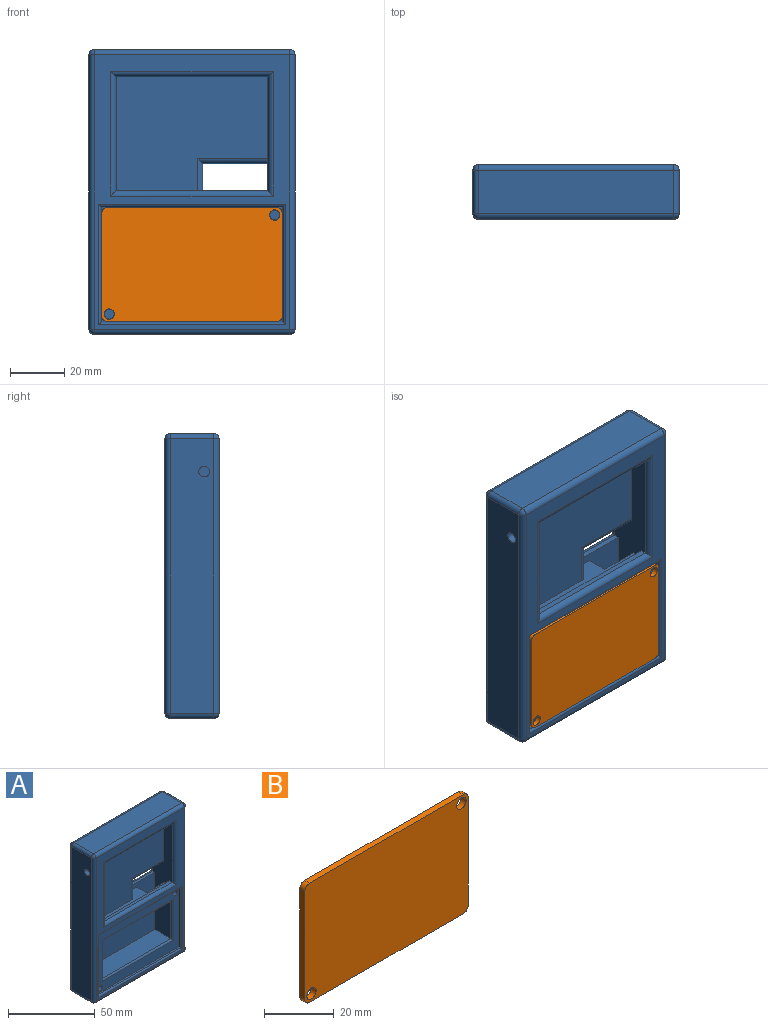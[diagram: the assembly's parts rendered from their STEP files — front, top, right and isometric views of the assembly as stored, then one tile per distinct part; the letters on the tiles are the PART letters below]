
ASSEMBLY  parts=2 mates=1
PART A: 70 faces, bbox 76x20x105 mm
  f0: plane 101x72mm, normal (0,-1,0), area 1441.5mm2, adj f29,f30,f39,f40,f46,f47,f48,f49
  f1: plane 24x2mm, normal (0,0,1), area 48mm2, adj f8,f17,f18,f24
  f2: plane 10.5x8mm, normal (1,0,0), area 84mm2, adj f3,f7,f17,f51
  f3: plane 15x10.5mm, normal (0,1,0), area 157.5mm2, adj f2,f7,f8,f51
  f4: plane 56x45mm, normal (0,-1,0), area 2130mm2, adj f8,f9,f10,f20,f21,f51
  f5: plane 101x72mm, normal (0,1,0), area 6880mm2, adj f22,f23,f24,f25,f32,f33,f41,f42
  f6: plane 27x13mm, normal (1,0,0), area 351mm2, adj f7,f16,f17,f63
  f7: plane 56x13mm, normal (0,0,-1), area 608mm2, adj f2,f3,f6,f8,f17,f62
  f8: plane 82.5x16mm, normal (-1,0,0), area 855.9mm2, adj f1,f3,f4,f7,f10,f14,f16,f17
  f9: plane 45x7mm, normal (1,0,0), area 296.4mm2, adj f4,f10,f14,f47,f50,f51,f52
  f10: plane 56x7mm, normal (0,0,-1), area 392mm2, adj f4,f8,f9,f46
  f11: plane 101x16mm, normal (1,0,0), area 1616mm2, adj f34,f39,f42,f45
  f12: plane 72x16mm, normal (0,0,1), area 1152mm2, adj f31,f40,f41,f45
  f13: plane 101x16mm, normal (-1,0,0), area 1603.4mm2, adj f26,f30,f31,f32,f52
  f14: plane 56x2mm, normal (0,0,1), area 112mm2, adj f8,f9,f49,f50
  f15: plane 72x16mm, normal (0,0,-1), area 1152mm2, adj f26,f29,f33,f34
  f16: plane 56x13mm, normal (0,0,1), area 728mm2, adj f6,f8,f17,f65
  f17: plane 56x40.5mm, normal (0,-1,0), area 1741.5mm2, adj f1,f2,f6,f7,f8,f16,f18,f51
  f18: plane 13x7mm, normal (1,0,0), area 85mm2, adj f1,f17,f19,f21,f22,f51
  f19: plane 24x7mm, normal (0,0,-1), area 168mm2, adj f8,f18,f20,f23
  f20: cylinder r=2mm len=26mm, axis (1,0,0), area 77.7mm2, adj f4,f8,f19,f21
  f21: cylinder r=2mm len=15mm, axis (0,0,1), area 43.1mm2, adj f4,f18,f20,f51
  f22: cylinder r=2mm len=14mm, axis (0,0,-1), area 36mm2, adj f5,f18,f23,f24
  f23: cylinder r=2mm len=28mm, axis (-1,0,0), area 80mm2, adj f5,f19,f22,f25
  f24: cylinder r=2mm len=28mm, axis (-1,0,0), area 80mm2, adj f1,f5,f22,f25
  f25: cylinder r=2mm len=14mm, axis (0,0,-1), area 36mm2, adj f5,f8,f23,f24
  f26: cylinder r=2mm len=16mm, axis (0,-1,0), area 50.3mm2, adj f13,f15,f27,f28
  f27: sphere r=2mm, area 6.3mm2, adj f26,f29,f30
  f28: sphere r=2mm, area 6.3mm2, adj f26,f32,f33
  f29: cylinder r=2mm len=72mm, axis (-1,0,0), area 226.2mm2, adj f0,f15,f27,f35
  f30: cylinder r=2mm len=101mm, axis (0,0,1), area 317.3mm2, adj f0,f13,f27,f36
  f31: cylinder r=2mm len=16mm, axis (0,1,0), area 50.3mm2, adj f12,f13,f36,f37
  f32: cylinder r=2mm len=101mm, axis (0,0,-1), area 317.3mm2, adj f5,f13,f28,f37
  f33: cylinder r=2mm len=72mm, axis (1,0,0), area 226.2mm2, adj f5,f15,f28,f38
  f34: cylinder r=2mm len=16mm, axis (0,1,0), area 50.3mm2, adj f11,f15,f35,f38
  f35: sphere r=2mm, area 6.3mm2, adj f29,f34,f39
  f36: sphere r=2mm, area 6.3mm2, adj f30,f31,f40
  f37: sphere r=2mm, area 6.3mm2, adj f31,f32,f41
  f38: sphere r=2mm, area 6.3mm2, adj f33,f34,f42
  f39: cylinder r=2mm len=101mm, axis (0,0,-1), area 317.3mm2, adj f0,f11,f35,f43
  f40: cylinder r=2mm len=72mm, axis (1,0,0), area 226.2mm2, adj f0,f12,f36,f43
  f41: cylinder r=2mm len=72mm, axis (-1,0,0), area 226.2mm2, adj f5,f12,f37,f44
  f42: cylinder r=2mm len=101mm, axis (0,0,1), area 317.3mm2, adj f5,f11,f38,f44
  f43: sphere r=2mm, area 6.3mm2, adj f39,f40,f45
  f44: sphere r=2mm, area 6.3mm2, adj f41,f42,f45
  f45: cylinder r=2mm len=16mm, axis (0,-1,0), area 50.3mm2, adj f11,f12,f43,f44
  f46: cylinder r=2mm len=60mm, axis (-1,0,0), area 180.5mm2, adj f0,f10,f47,f48
  f47: cylinder r=2mm len=46mm, axis (0,0,-1), area 136.5mm2, adj f0,f9,f46,f49
  f48: cylinder r=2mm len=46mm, axis (0,0,1), area 136.5mm2, adj f0,f8,f46,f49
  f49: cylinder r=2mm len=60mm, axis (1,0,0), area 180.5mm2, adj f0,f14,f47,f48
  f50: plane 56x3mm, normal (0,1,0), area 168mm2, adj f8,f9,f14,f51
  f51: plane 56x12mm, normal (0,0,1), area 328.9mm2, adj f2,f3,f4,f8,f9,f17,f18,f21
  f52: cylinder r=2mm len=10mm, axis (-1,0,0), area 125.7mm2, adj f9,f13
  f53: plane 67x1mm, normal (0,0,-1), area 67mm2, adj f54,f56,f57,f58
  f54: plane 42.5x1mm, normal (1,0,0), area 42.5mm2, adj f53,f55,f57,f59
  f55: plane 67x1mm, normal (0,0,1), area 67mm2, adj f54,f56,f57,f61
  f56: plane 42.5x1mm, normal (-1,0,0), area 42.5mm2, adj f53,f55,f57,f60
  f57: plane 67x42.5mm, normal (0,-1,0), area 1144.5mm2, adj f53,f54,f55,f56,f62,f63,f64,f65
  f58: cylinder r=1mm len=69mm, axis (1,0,0), area 106.4mm2, adj f0,f53,f59,f60
  f59: cylinder r=1mm len=44.5mm, axis (0,0,1), area 67.9mm2, adj f0,f54,f58,f61
  f60: cylinder r=1mm len=44.5mm, axis (0,0,-1), area 67.9mm2, adj f0,f56,f58,f61
  f61: cylinder r=1mm len=69mm, axis (-1,0,0), area 106.4mm2, adj f0,f55,f59,f60
  f62: cylinder r=1mm len=58mm, axis (1,0,0), area 89.1mm2, adj f7,f57,f63,f64
  f63: cylinder r=1mm len=29mm, axis (0,0,-1), area 43.6mm2, adj f6,f57,f62,f65
  f64: cylinder r=1mm len=29mm, axis (0,0,-1), area 43.6mm2, adj f8,f57,f62,f65
  f65: cylinder r=1mm len=58mm, axis (1,0,0), area 89.1mm2, adj f16,f57,f63,f64
  f66: cylinder r=1.83mm len=6mm, axis (0,-1,0), area 68.9mm2, adj f57,f67
  f67: plane 3.66x3.66mm, normal (0,-1,0), area 10.5mm2, adj f66
  f68: cylinder r=1.83mm len=6mm, axis (0,-1,0), area 68.9mm2, adj f57,f69
  f69: plane 3.66x3.66mm, normal (0,-1,0), area 10.5mm2, adj f68
PART B: 12 faces, bbox 66.5x2x42 mm
  f0: plane 38x2mm, normal (1,0,0), area 76mm2, adj f4,f5,f8,f11
  f1: plane 62.5x2mm, normal (0,0,1), area 125mm2, adj f4,f5,f8,f9
  f2: plane 38x2mm, normal (-1,0,0), area 76mm2, adj f4,f5,f9,f10
  f3: plane 62.5x2mm, normal (0,0,-1), area 125mm2, adj f4,f5,f10,f11
  f4: plane 66.5x42mm, normal (0,-1,0), area 2766.9mm2, adj f0,f1,f2,f3,f6,f7,f8,f9
  f5: plane 66.5x42mm, normal (0,1,0), area 2766.9mm2, adj f0,f1,f2,f3,f6,f7,f8,f9
  f6: cylinder r=1.9mm len=3.8mm, axis (0,-1,0), area 23.9mm2, adj f4,f5
  f7: cylinder r=1.9mm len=3.8mm, axis (0,-1,0), area 23.9mm2, adj f4,f5
  f8: cylinder r=2mm len=2mm, axis (0,-1,0), area 6.3mm2, adj f0,f1,f4,f5
  f9: cylinder r=2mm len=2mm, axis (0,1,0), area 6.3mm2, adj f1,f2,f4,f5
  f10: cylinder r=2mm len=2mm, axis (0,-1,0), area 6.3mm2, adj f2,f3,f4,f5
  f11: cylinder r=2mm len=2mm, axis (0,1,0), area 6.3mm2, adj f0,f3,f4,f5
PLACE A t=(37.74,-44.8,18.06)mm
PLACE B t=(37.74,-63.8,-8.69)mm
MATE fastened B.f7 <-> A.f68  axis (0,1,0) through (7.24,-62.8,-26.94)mm
